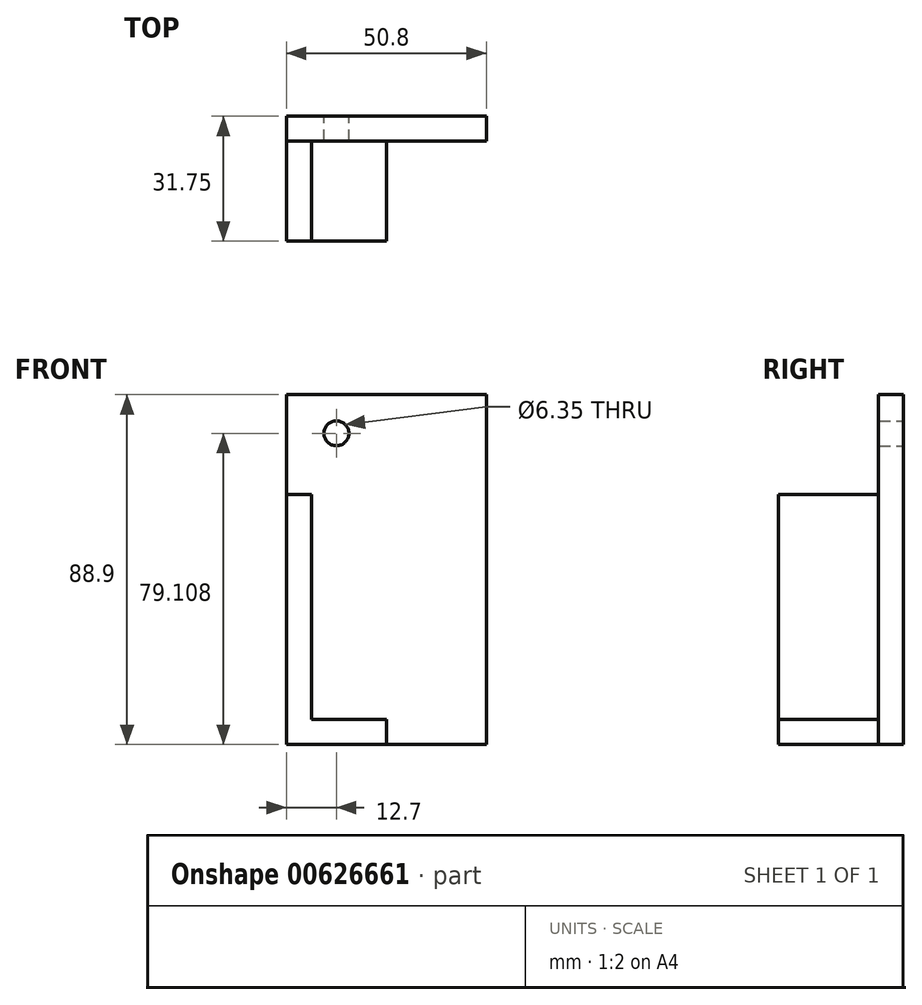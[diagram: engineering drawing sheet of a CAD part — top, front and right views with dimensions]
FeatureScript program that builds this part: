
annotation { "Feature Type Name" : "Feature", "Feature Type Description" : "" }
export const myFeature = defineFeature(function(context is Context, id is Id, definition is map)
    precondition{}
    {
        {
            var Q0;
            Q0=qCreatedBy(makeId("Front.planeOp"),FACE);
            var sketch = newSketch(context, id + "F0", { "sketchPlane" : qUnion([Q0])});
            skLineSegment(sketch, "E0.bottom", {"start": v(25.4, 44.45) * mm, "end": v(-25.4, 44.45) * mm});
            skLineSegment(sketch, "E0.top", {"start": v(25.4, -44.45) * mm, "end": v(-25.4, -44.45) * mm});
            skLineSegment(sketch, "E0.left", {"start": v(25.4, 44.45) * mm, "end": v(25.4, -44.45) * mm});
            skLineSegment(sketch, "E0.right", {"start": v(-25.4, 44.45) * mm, "end": v(-25.4, -44.45) * mm});
            skPoint(sketch, "E0.middle", {"position": v(0, 0) * mm});
            skSolve(sketch);
        }
        {
            var Q0;
            Q0=makeQuery(id+"F0.imprint","IMPRINT",FACE,{"disambiguationData":[TD([[makeQuery(id+"F0.imprint","IMPRINT",EDGE,{"derivedFrom":sQuery(id+"F0.wireOp",EDGE,"E0.bottom")}),1.0]])]});
            extrude(context, id + "F1", {"entities" : qUnion([Q0]), "depth" : 31.75 * mm, "offsetDistance" : 25.4 * mm});
        }
        {
            var Q0;
            Q0=makeQuery(id+"F1.opExtrude","SWEPT_FACE",FACE,{"disambiguationData":[OSD([sQuery(id+"F0.wireOp",EDGE,"E0.left")])]});
            var sketch = newSketch(context, id + "F2", { "sketchPlane" : qUnion([Q0])});
            skLineSegment(sketch, "E1.bottom", {"start": v(-31.75, 44.45) * mm, "end": v(-6.35, 44.45) * mm});
            skLineSegment(sketch, "E1.top", {"start": v(-31.75, -38.1) * mm, "end": v(-6.35, -38.1) * mm});
            skLineSegment(sketch, "E1.left", {"start": v(-31.75, 44.45) * mm, "end": v(-31.75, -38.1) * mm});
            skLineSegment(sketch, "E1.right", {"start": v(-6.35, 44.45) * mm, "end": v(-6.35, -38.1) * mm});
            skSolve(sketch);
        }
        {
            var Q0;
            Q0=makeQuery(id+"F2.imprint","IMPRINT",FACE,{"disambiguationData":[TD([[makeQuery(id+"F2.imprint","IMPRINT",EDGE,{"derivedFrom":sQuery(id+"F2.wireOp",EDGE,"E1.bottom")}),-1.0]])]});
            extrude(context, id + "F3", {"entities" : qUnion([Q0]), "operationType" : NewBodyOperationType.REMOVE, "oppositeDirection" : true, "depth" : 44.45 * mm, "offsetDistance" : 25.4 * mm});
        }
        {
            var Q0;
            Q0=makeQuery(id+"F1.opExtrude","SWEPT_FACE",FACE,{"disambiguationData":[OSD([sQuery(id+"F0.wireOp",EDGE,"E0.right")])]});
            var sketch = newSketch(context, id + "F4", { "sketchPlane" : qUnion([Q0])});
            skLineSegment(sketch, "E2.bottom", {"start": v(31.75, 44.45) * mm, "end": v(6.35, 44.45) * mm});
            skLineSegment(sketch, "E2.top", {"start": v(31.75, 19.05) * mm, "end": v(6.35, 19.05) * mm});
            skLineSegment(sketch, "E2.left", {"start": v(31.75, 44.45) * mm, "end": v(31.75, 19.05) * mm});
            skLineSegment(sketch, "E2.right", {"start": v(6.35, 44.45) * mm, "end": v(6.35, 19.05) * mm});
            skSolve(sketch);
        }
        {
            var Q0;
            Q0=makeQuery(id+"F4.imprint","IMPRINT",FACE,{"disambiguationData":[TD([[makeQuery(id+"F4.imprint","IMPRINT",EDGE,{"derivedFrom":sQuery(id+"F4.wireOp",EDGE,"E2.bottom")}),1.0]])]});
            extrude(context, id + "F5", {"entities" : qUnion([Q0]), "operationType" : NewBodyOperationType.REMOVE, "oppositeDirection" : true, "depth" : 25.4 * mm, "offsetDistance" : 25.4 * mm});
        }
        {
            var Q0;
            Q0=makeQuery(id+"F1.opExtrude","CAP_FACE",FACE,{"disambiguationData":[OSD([sQuery(id+"F0.wireOp",EDGE,"E0.bottom"),sQuery(id+"F0.wireOp",EDGE,"E0.top"),sQuery(id+"F0.wireOp",EDGE,"E0.left"),sQuery(id+"F0.wireOp",EDGE,"E0.right")])],"isStart":false});
            var sketch = newSketch(context, id + "F6", { "sketchPlane" : qUnion([Q0])});
            skLineSegment(sketch, "E3.bottom", {"start": v(25.4, -38.1) * mm, "end": v(0, -38.1) * mm});
            skLineSegment(sketch, "E3.top", {"start": v(25.4, -44.45) * mm, "end": v(0, -44.45) * mm});
            skLineSegment(sketch, "E3.left", {"start": v(25.4, -38.1) * mm, "end": v(25.4, -44.45) * mm});
            skLineSegment(sketch, "E3.right", {"start": v(0, -38.1) * mm, "end": v(0, -44.45) * mm});
            skSolve(sketch);
        }
        {
            var Q0;
            Q0=makeQuery(id+"F6.imprint","IMPRINT",FACE,{"disambiguationData":[TD([[makeQuery(id+"F6.imprint","IMPRINT",EDGE,{"derivedFrom":sQuery(id+"F6.wireOp",EDGE,"E3.bottom")}),-1.0]])]});
            extrude(context, id + "F7", {"entities" : qUnion([Q0]), "operationType" : NewBodyOperationType.REMOVE, "oppositeDirection" : true, "depth" : 25.4 * mm, "offsetDistance" : 25.4 * mm});
        }
        {
            var Q0;
            Q0=makeQuery(id+"F1.opExtrude","CAP_FACE",FACE,{"disambiguationData":[OSD([sQuery(id+"F0.wireOp",EDGE,"E0.bottom"),sQuery(id+"F0.wireOp",EDGE,"E0.top"),sQuery(id+"F0.wireOp",EDGE,"E0.left"),sQuery(id+"F0.wireOp",EDGE,"E0.right")])],"isStart":true});
            var sketch = newSketch(context, id + "F8", { "sketchPlane" : qUnion([Q0])});
            skCircle(sketch, "E4", {"center": v(12.7, 34.66) * mm, "radius": 3.18 * mm});
            skSolve(sketch);
        }
        {
            var Q0;
            Q0=makeQuery(id+"F8.imprint","IMPRINT",FACE,{"disambiguationData":[TD([[makeQuery(id+"F8.imprint","IMPRINT",EDGE,{"derivedFrom":sQuery(id+"F8.wireOp",EDGE,"E4")}),1.0]])]});
            extrude(context, id + "F9", {"entities" : qUnion([Q0]), "operationType" : NewBodyOperationType.REMOVE, "oppositeDirection" : true, "depth" : 25.4 * mm, "offsetDistance" : 25.4 * mm});
        }
    });
